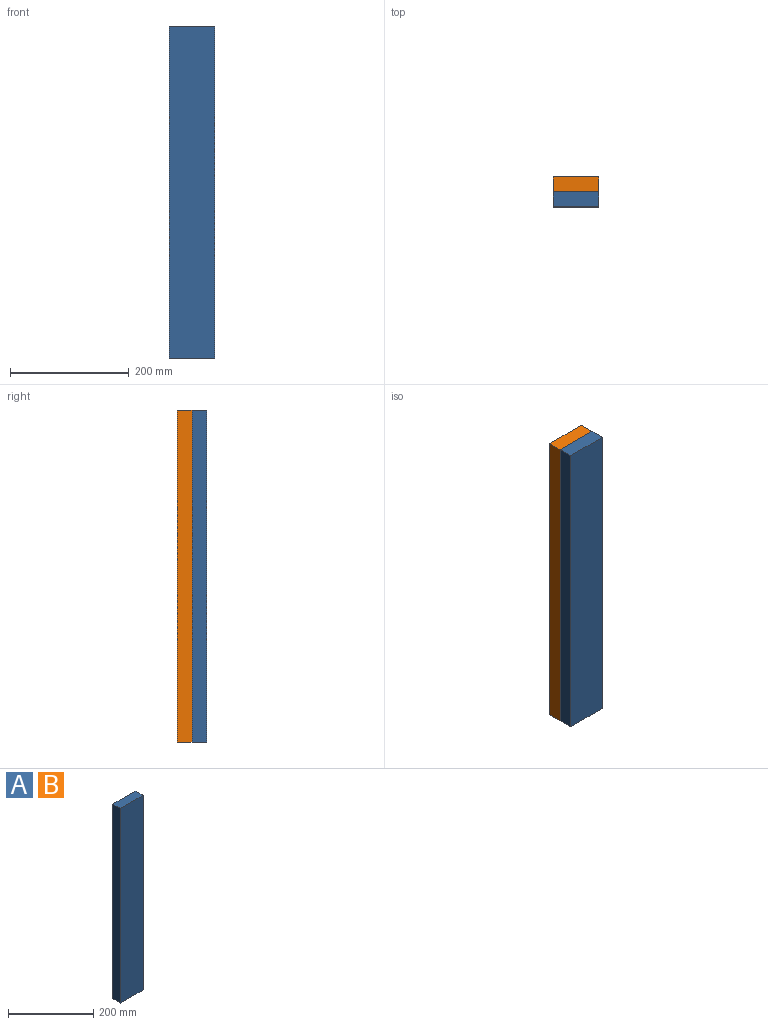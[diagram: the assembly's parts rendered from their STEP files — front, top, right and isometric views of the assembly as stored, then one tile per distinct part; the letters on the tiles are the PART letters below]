
ASSEMBLY  parts=2 mates=1
PART A: 6 faces, bbox 76x25x560 mm
  f0: plane 76x25mm, normal (0,0,1), area 1900mm2, adj f1,f3,f4,f5
  f1: plane 560x25mm, normal (-1,0,0), area 14000mm2, adj f0,f2,f4,f5
  f2: plane 76x25mm, normal (0,0,-1), area 1900mm2, adj f1,f3,f4,f5
  f3: plane 560x25mm, normal (1,0,0), area 14000mm2, adj f0,f2,f4,f5
  f4: plane 560x76mm, normal (0,-1,0), area 42560mm2, adj f0,f1,f2,f3
  f5: plane 560x76mm, normal (0,1,0), area 42560mm2, adj f0,f1,f2,f3
PART B: same geometry as A
PLACE A t=(0,-75,0)mm
PLACE B t=(0,-50,0)mm
MATE fastened A.f5 <-> B.f4  axis (0,1,0) through (-26.7,-75,271.24)mm
